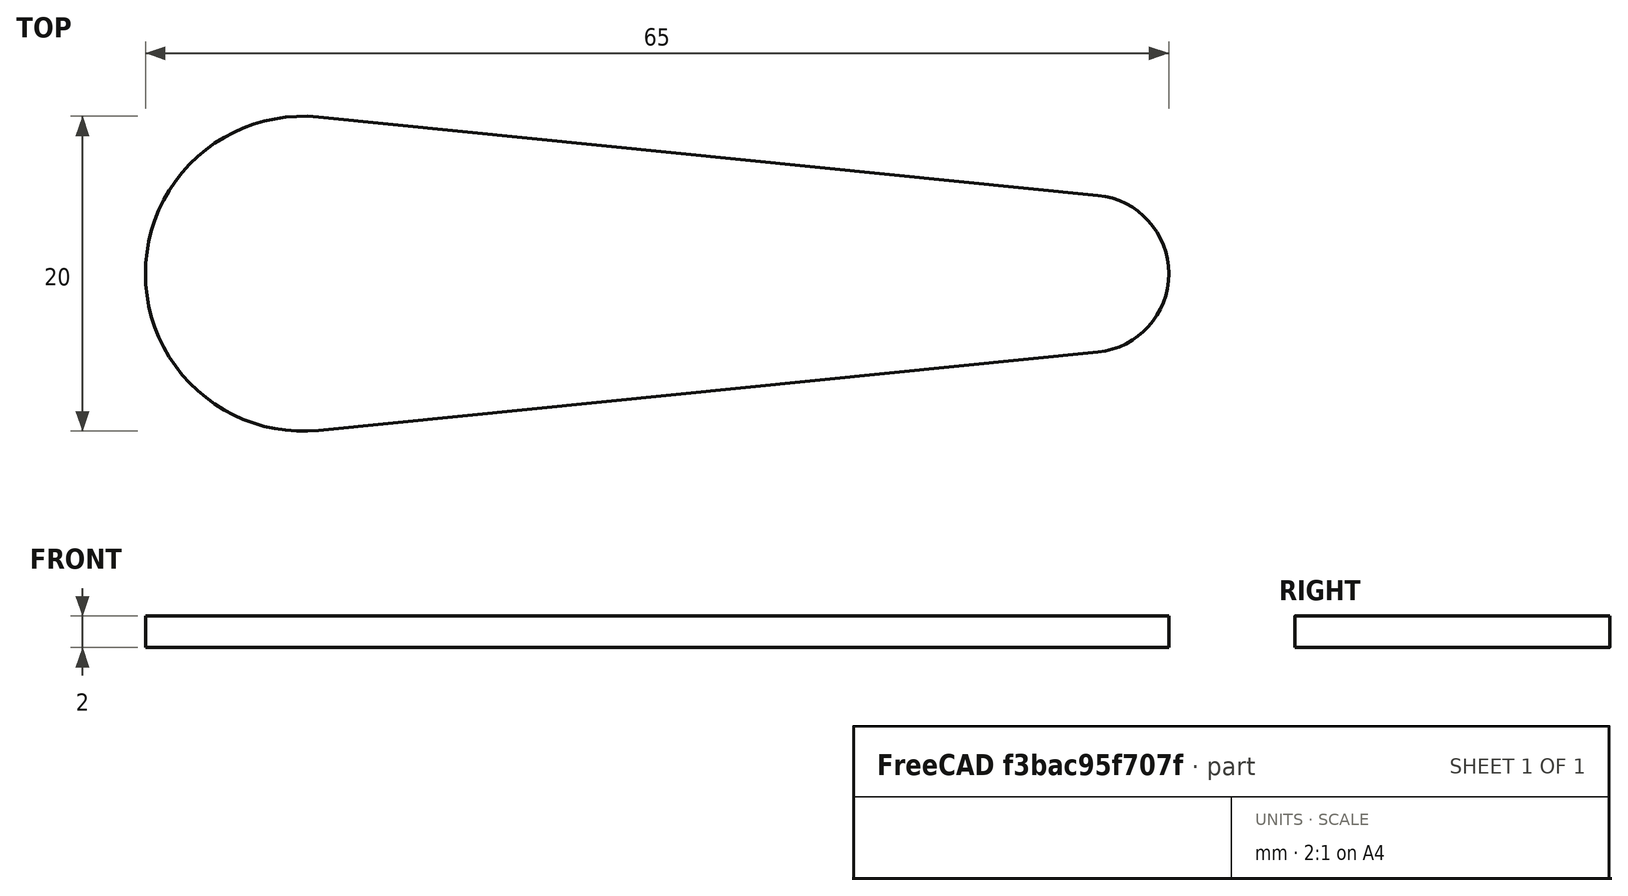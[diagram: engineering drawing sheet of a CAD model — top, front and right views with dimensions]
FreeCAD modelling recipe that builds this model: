
FCSTD DOCUMENT  (FreeCAD 0.22R38495 (Git))
Label: Filament Oozing Remover
License: Creative Commons Attribution-ShareAlike 4.0
LicenseURL: https://creativecommons.org/licenses/by-sa/4.0/
objects: Sketcher::SketchObject×1, PartDesign::Pad×1, PartDesign::Body×1, App::Part×1
note: 6 computed .brp shape members not serialized (recipe doc carries the construction recipe); baked Part::Feature solids carry a one-line shape summary decoded from their .brp

FEATURE [Sketcher::SketchObject] Sketch  label="Base"
  ArcFitTolerance = 1e-06
  AttachmentSupport = -> [XY_Plane001]
  FullyConstrained = true
  MakeInternals = false
  MapMode = 5
  sketch-geometry (4):
    g0: ArcOfCircle CenterX=0 CenterY=0 CenterZ=0 NormalX=0 NormalY=0 NormalZ=1 AngleXU=0 Radius=10 StartAngle=1.47063 EndAngle=4.81256
    g1: ArcOfCircle CenterX=50 CenterY=0 CenterZ=0 NormalX=0 NormalY=0 NormalZ=1 AngleXU=0 Radius=5 StartAngle=4.81256 EndAngle=7.75381
    g2: LineSegment StartX=1 StartY=9.94987 StartZ=0 EndX=50.5 EndY=4.97494 EndZ=0
    g3: LineSegment StartX=1 StartY=-9.94987 StartZ=0 EndX=50.5 EndY=-4.97494 EndZ=0
  constraints (9):
    c: Diameter(g0) = 20
    c: Coincident(g0,g-1)
    c: Diameter(g1) = 10
    c: PointOnObject(g1,g-1)
    c: DistanceX(g0,g1) = 50
    c: Tangent(g0,g3) = -1.5708
    c: Tangent(g0,g2) = 1.5708
    c: Tangent(g1,g2) = 1.5708
    c: Tangent(g1,g3) = -1.5708
FEATURE [PartDesign::Pad] Pad  label="The Tool"
  Direction = (0,0,1)
  Length = 2
  Length2 = 10
  Profile = -> Sketch
  ReferenceAxis = -> Sketch [N_Axis]
  Refine = true
  Suppressed = false
  Type = 0
FEATURE [PartDesign::Body] Body  label="The Tool"
  AllowCompound = false
  Group = -> [Sketch,Pad]
  Origin = -> Origin001
  Tip = -> Pad
FEATURE [App::Part] Part  label="Filament Oozing Remover"
  Group = -> [Body]
  Origin = -> Origin
